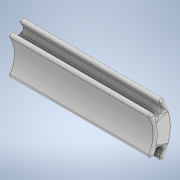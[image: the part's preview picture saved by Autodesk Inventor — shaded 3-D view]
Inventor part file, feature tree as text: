
AUTODESK INVENTOR PART (.ipt)
format: ipt  version: 2020 (Build 240168000, 168)  size: 240,640 bytes
history: native  units: in
note: dims shown in document units (in); Inventor stores cm internally (conversion verified against a paired STEP export)
features: fillet x4, extrude x1, sketch x1
ambient origin geometry x8: Origin, YZ Plane, XZ Plane, XY Plane, X Axis, Y Axis, Z Axis, Center Point
bodies: Solid1 (feature_tree)
feature tree (6):
  extrude  "Extrusion1"  Depth=0.0787in
  fillet  "Fillet1"  Radius=0.481in
  fillet  "Fillet2"  Radius=0.0197in
  fillet  "Fillet3"  Radius=0.0197in
  fillet  "Fillet4"  Radius=0.0197in
  sketch  "Sketch1"  dims[d0=1.1811in d1=0.0787in d2=0.481in d3=0.0197in d4=0.0197in d5=0.0197in d6=0.0197in d7=0.0591in d8=0.0591in d9=0.0591in d10=0.0591in d11=0.0591in d12=0.0591in d13=1.9685in d14=0.0in d15=0.0295in d16=0.0295in d17=0.0295in d18=0.0472in]
